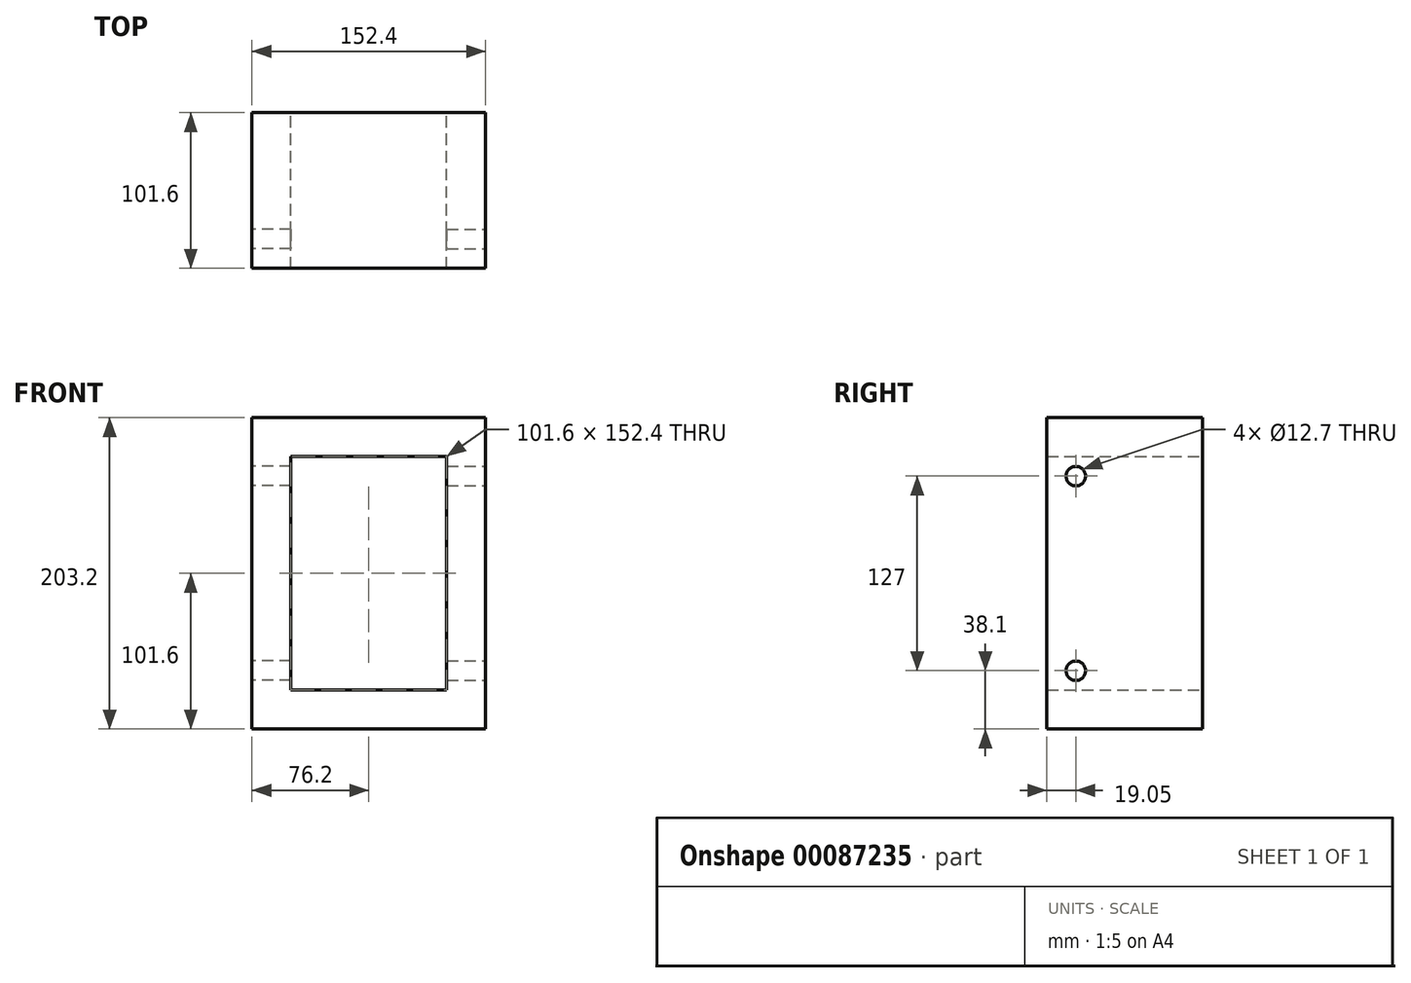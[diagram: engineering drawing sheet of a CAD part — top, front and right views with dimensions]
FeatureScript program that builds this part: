
annotation { "Feature Type Name" : "Feature", "Feature Type Description" : "" }
export const myFeature = defineFeature(function(context is Context, id is Id, definition is map)
    precondition{}
    {
        {
            var Q0;
            Q0=qCreatedBy(makeId("Front.planeOp"),FACE);
            var sketch = newSketch(context, id + "F0", { "sketchPlane" : qUnion([Q0])});
            skLineSegment(sketch, "E0.bottom", {"start": v(-76.2, 101.6) * mm, "end": v(76.2, 101.6) * mm});
            skLineSegment(sketch, "E0.top", {"start": v(-76.2, -101.6) * mm, "end": v(76.2, -101.6) * mm});
            skLineSegment(sketch, "E0.left", {"start": v(-76.2, 101.6) * mm, "end": v(-76.2, -101.6) * mm});
            skLineSegment(sketch, "E0.right", {"start": v(76.2, 101.6) * mm, "end": v(76.2, -101.6) * mm});
            skLineSegment(sketch, "E1.bottom", {"start": v(-50.8, 76.2) * mm, "end": v(50.8, 76.2) * mm});
            skLineSegment(sketch, "E1.top", {"start": v(-50.8, -76.2) * mm, "end": v(50.8, -76.2) * mm});
            skLineSegment(sketch, "E1.left", {"start": v(-50.8, 76.2) * mm, "end": v(-50.8, -76.2) * mm});
            skLineSegment(sketch, "E1.right", {"start": v(50.8, 76.2) * mm, "end": v(50.8, -76.2) * mm});
            skLineSegment(sketch, "E2", {"start": v(0, 76.2) * mm, "end": v(0, -76.2) * mm, "construction": true});
            skLineSegment(sketch, "E3", {"start": v(0, 76.2) * mm, "end": v(0, 101.6) * mm, "construction": true});
            skLineSegment(sketch, "E4", {"start": v(0, -76.2) * mm, "end": v(0, -101.6) * mm, "construction": true});
            skLineSegment(sketch, "E5", {"start": v(0, 0) * mm, "end": v(-50.8, 0) * mm, "construction": true});
            skLineSegment(sketch, "E6", {"start": v(0, 0) * mm, "end": v(50.8, 0) * mm, "construction": true});
            skLineSegment(sketch, "E7", {"start": v(-50.8, 0) * mm, "end": v(-76.2, 0) * mm, "construction": true});
            skLineSegment(sketch, "E8", {"start": v(50.8, 0) * mm, "end": v(76.2, 0) * mm, "construction": true});
            skSolve(sketch);
        }
        {
            var Q0;
            Q0=makeQuery(id+"F0.imprint","IMPRINT",FACE,{"disambiguationData":[TD([[makeQuery(id+"F0.imprint","IMPRINT",EDGE,{"derivedFrom":sQuery(id+"F0.wireOp",EDGE,"E0.bottom")}),-1.0]])]});
            extrude(context, id + "F1", {"entities" : qUnion([Q0]), "depth" : 101.6 * mm});
        }
        {
            var Q0;
            Q0=makeQuery(id+"F1.opExtrude","SWEPT_FACE",FACE,{"disambiguationData":[OSD([sQuery(id+"F0.wireOp",EDGE,"E0.left")])]});
            var sketch = newSketch(context, id + "F2", { "sketchPlane" : qUnion([Q0])});
            skCircle(sketch, "E9", {"center": v(82.55, -63.5) * mm, "radius": 6.35 * mm});
            skCircle(sketch, "E10", {"center": v(82.55, 63.5) * mm, "radius": 6.35 * mm});
            skLineSegment(sketch, "E11", {"start": v(82.55, 63.5) * mm, "end": v(82.55, -63.5) * mm, "construction": true});
            skLineSegment(sketch, "E12", {"start": v(0, 0) * mm, "end": v(82.55, 0) * mm, "construction": true});
            skPoint(sketch, "E13", {"position": v(101.6, 0) * mm});
            skCircle(sketch, "E14", {"center": v(82.55, 63.5) * mm, "radius": 44.45 * mm, "construction": true});
            skSolve(sketch);
        }
        {
            var Q0;
            Q0 = qSketchRegion(id + "F2", true);
            extrude(context, id + "F3", {"entities" : qUnion([Q0]), "operationType" : NewBodyOperationType.REMOVE, "oppositeDirection" : true, "depth" : 25.4 * mm});
        }
        {
            var Q0;
            Q0=makeQuery(id+"F1.opExtrude","SWEPT_FACE",FACE,{"disambiguationData":[OSD([sQuery(id+"F0.wireOp",EDGE,"E0.right")])]});
            var sketch = newSketch(context, id + "F4", { "sketchPlane" : qUnion([Q0])});
            skLineSegment(sketch, "E15", {"start": v(0, 0) * mm, "end": v(-82.55, 0) * mm, "construction": true});
            skPoint(sketch, "E15.endSnap0", {"position": v(0, 0) * mm});
            skLineSegment(sketch, "E16", {"start": v(-82.55, 63.5) * mm, "end": v(-82.55, -63.5) * mm, "construction": true});
            skCircle(sketch, "E17", {"center": v(-82.55, 63.5) * mm, "radius": 6.35 * mm});
            skCircle(sketch, "E18", {"center": v(-82.55, -63.5) * mm, "radius": 6.35 * mm});
            skSolve(sketch);
        }
        {
            var Q0;
            Q0 = qSketchRegion(id + "F4", true);
            extrude(context, id + "F5", {"entities" : qUnion([Q0]), "operationType" : NewBodyOperationType.REMOVE, "oppositeDirection" : true, "depth" : 25.4 * mm});
        }
    });
